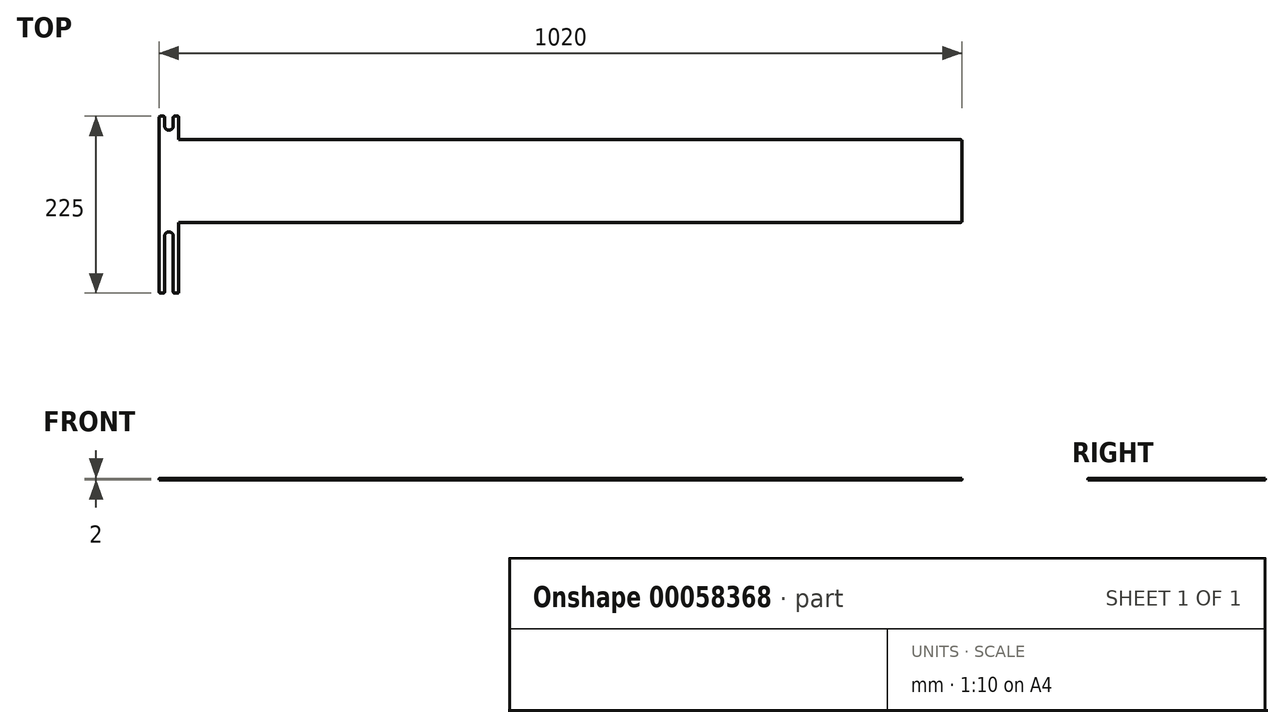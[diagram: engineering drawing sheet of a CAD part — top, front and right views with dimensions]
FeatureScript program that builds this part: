
annotation { "Feature Type Name" : "Feature", "Feature Type Description" : "" }
export const myFeature = defineFeature(function(context is Context, id is Id, definition is map)
    precondition{}
    {
        {
            var Q0;
            Q0=qCreatedBy(makeId("Top.planeOp"),FACE);
            var sketch = newSketch(context, id + "F0", { "sketchPlane" : qUnion([Q0])});
            skLineSegment(sketch, "E0.bottom", {"start": v(-510, 52.5) * mm, "end": v(510, 52.5) * mm});
            skLineSegment(sketch, "E0.top", {"start": v(-510, -52.5) * mm, "end": v(510, -52.5) * mm});
            skLineSegment(sketch, "E0.left", {"start": v(-510, 52.5) * mm, "end": v(-510, -52.5) * mm});
            skLineSegment(sketch, "E0.right", {"start": v(510, 52.5) * mm, "end": v(510, -52.5) * mm});
            skSolve(sketch);
        }
        {
            var Q0;
            Q0=makeQuery(id+"F0.imprint","IMPRINT",FACE,{"disambiguationData":[TD([[makeQuery(id+"F0.imprint","IMPRINT",EDGE,{"derivedFrom":sQuery(id+"F0.wireOp",EDGE,"E0.bottom")}),-1.0]])]});
            extrude(context, id + "F1", {"entities" : qUnion([Q0]), "depth" : 2 * mm});
        }
        {
            var Q0;
            Q0=makeQuery(id+"F1.opExtrude","CAP_FACE",FACE,{"disambiguationData":[OSD([sQuery(id+"F0.wireOp",EDGE,"E0.bottom"),sQuery(id+"F0.wireOp",EDGE,"E0.top"),sQuery(id+"F0.wireOp",EDGE,"E0.left"),sQuery(id+"F0.wireOp",EDGE,"E0.right")])],"isStart":false});
            var sketch = newSketch(context, id + "F2", { "sketchPlane" : qUnion([Q0])});
            skLineSegment(sketch, "E1", {"start": v(-510, -52.5) * mm, "end": v(-510, -142.5) * mm});
            skLineSegment(sketch, "E2", {"start": v(-510, -142.5) * mm, "end": v(-503, -142.5) * mm});
            skLineSegment(sketch, "E3", {"start": v(-503, -142.5) * mm, "end": v(-503, -64.5) * mm});
            skLineSegment(sketch, "E4", {"start": v(-503, -64.5) * mm, "end": v(-492.1, -64.5) * mm});
            skLineSegment(sketch, "E5", {"start": v(-492.1, -64.5) * mm, "end": v(-492.1, -142.5) * mm});
            skLineSegment(sketch, "E6", {"start": v(-492.1, -142.5) * mm, "end": v(-485, -142.5) * mm});
            skLineSegment(sketch, "E7", {"start": v(-485, -142.5) * mm, "end": v(-485, -52.5) * mm});
            skLineSegment(sketch, "E8", {"start": v(-485, -52.5) * mm, "end": v(-510, -52.5) * mm});
            skSolve(sketch);
        }
        {
            var Q0;
            Q0=makeQuery(id+"F2.imprint","IMPRINT",FACE,{"disambiguationData":[TD([[makeQuery(id+"F2.imprint","IMPRINT",EDGE,{"derivedFrom":sQuery(id+"F2.wireOp",EDGE,"E1")}),1.0]])]});
            extrude(context, id + "F3", {"entities" : qUnion([Q0]), "operationType" : NewBodyOperationType.ADD, "oppositeDirection" : true, "depth" : 2 * mm});
        }
        {
            var Q0;
            Q0=makeQuery(id+"F3.boolean.opBoolean","MERGE",FACE,{"derivedFrom":[makeQuery(id+"F1.opExtrude","CAP_FACE",FACE,{"disambiguationData":[OSD([sQuery(id+"F0.wireOp",EDGE,"E0.bottom"),sQuery(id+"F0.wireOp",EDGE,"E0.top"),sQuery(id+"F0.wireOp",EDGE,"E0.left"),sQuery(id+"F0.wireOp",EDGE,"E0.right")])],"isStart":false}),makeQuery(id+"F3.opExtrude","CAP_FACE",FACE,{"disambiguationData":[OSD([sQuery(id+"F2.wireOp",EDGE,"E1"),sQuery(id+"F2.wireOp",EDGE,"E2"),sQuery(id+"F2.wireOp",EDGE,"E3"),sQuery(id+"F2.wireOp",EDGE,"E4"),sQuery(id+"F2.wireOp",EDGE,"E5"),sQuery(id+"F2.wireOp",EDGE,"E6"),sQuery(id+"F2.wireOp",EDGE,"E7"),sQuery(id+"F2.wireOp",EDGE,"E8")])],"isStart":true})]});
            var sketch = newSketch(context, id + "F4", { "sketchPlane" : qUnion([Q0])});
            skLineSegment(sketch, "E9", {"start": v(0, 0) * mm, "end": v(-510, 0) * mm, "construction": true});
            skSolve(sketch);
        }
        {
            var Q0;
            Q0=makeQuery(id+"F1.opExtrude","SWEPT_BODY",BODY,{"disambiguationData":[OSD([sQuery(id+"F0.wireOp",EDGE,"E0.bottom"),sQuery(id+"F0.wireOp",EDGE,"E0.top"),sQuery(id+"F0.wireOp",EDGE,"E0.left"),sQuery(id+"F0.wireOp",EDGE,"E0.right")])]});
            var Q1;
            Q1=qCreatedBy(makeId("Front.planeOp"),FACE);
            mirror(context, id + "F5", {"operationType" : NewBodyOperationType.ADD, "entities" : qUnion([Q0]), "mirrorPlane" : qUnion([Q1])});
        }
        {
            var Q0;
            Q0=makeQuery(id+"F4.imprint","IMPRINT",FACE,{"disambiguationData":[TD([[makeQuery(id+"F4.imprint","IMPRINT",EDGE,{"derivedFrom":makeQuery(id+"F1.opExtrude","CAP_EDGE",EDGE,{"disambiguationData":[OSD([sQuery(id+"F0.wireOp",EDGE,"E0.bottom")])],"isStart":false})}),-1.0]])]});
            var sketch = newSketch(context, id + "F6", { "sketchPlane" : qUnion([Q0])});
            skLineSegment(sketch, "E10.bottom", {"start": v(-535.27, 162.5) * mm, "end": v(-465.98, 162.5) * mm});
            skLineSegment(sketch, "E10.top", {"start": v(-535.27, 82.5) * mm, "end": v(-465.98, 82.5) * mm});
            skLineSegment(sketch, "E10.left", {"start": v(-535.27, 162.5) * mm, "end": v(-535.27, 82.5) * mm});
            skLineSegment(sketch, "E10.right", {"start": v(-465.98, 162.5) * mm, "end": v(-465.98, 82.5) * mm});
            skSolve(sketch);
        }
        {
            var Q0;
            Q0=makeQuery(id+"F6.imprint","IMPRINT",FACE,{"disambiguationData":[TD([[makeQuery(id+"F6.imprint","IMPRINT",EDGE,{"derivedFrom":sQuery(id+"F6.wireOp",EDGE,"E10.bottom")}),-1.0]])]});
            extrude(context, id + "F7", {"entities" : qUnion([Q0]), "operationType" : NewBodyOperationType.REMOVE, "endBound" : BoundingType.THROUGH_ALL, "oppositeDirection" : true, "depth" : 25 * mm});
        }
        {
            var Q0;
            Q0=makeQuery(id+"F3.opExtrude","SWEPT_EDGE",EDGE,{"disambiguationData":[OSD([sQuery(id+"F2.wireOp",EDGE,"E3"),sQuery(id+"F2.wireOp",EDGE,"E4")])]});
            var Q1;
            Q1=makeQuery(id+"F3.opExtrude","SWEPT_EDGE",EDGE,{"disambiguationData":[OSD([sQuery(id+"F2.wireOp",EDGE,"E4"),sQuery(id+"F2.wireOp",EDGE,"E5")])]});
            var Q2;
            Q2=makeQuery(id+"F5.opPattern","COPY",EDGE,{"derivedFrom":makeQuery(id+"F3.opExtrude","SWEPT_EDGE",EDGE,{"disambiguationData":[OSD([sQuery(id+"F2.wireOp",EDGE,"E3"),sQuery(id+"F2.wireOp",EDGE,"E4")])]}),"instanceName":"1"});
            var Q3;
            Q3=makeQuery(id+"F5.opPattern","COPY",EDGE,{"derivedFrom":makeQuery(id+"F3.opExtrude","SWEPT_EDGE",EDGE,{"disambiguationData":[OSD([sQuery(id+"F2.wireOp",EDGE,"E4"),sQuery(id+"F2.wireOp",EDGE,"E5")])]}),"instanceName":"1"});
            fillet(context, id + "F8", {"entities" : qUnion([Q0, Q1, Q2, Q3]), "radius" : 5.45 * mm, "tangentPropagation" : true, "allowEdgeOverflow" : false});
        }
        {
            var Q0;
            Q0=makeQuery(id+"F5.opPattern","COPY",EDGE,{"derivedFrom":makeQuery(id+"F3.opExtrude","SWEPT_EDGE",EDGE,{"disambiguationData":[OSD([sQuery(id+"F0.wireOp",EDGE,"E0.top"),sQuery(id+"F2.wireOp",EDGE,"E7"),sQuery(id+"F2.wireOp",EDGE,"E8")])]}),"instanceName":"1"});
            var Q1;
            Q1=makeQuery(id+"F7.boolean.opBoolean","INTERSECT",EDGE,{"derivedFrom":[makeQuery(id+"F5.opPattern","COPY",FACE,{"derivedFrom":makeQuery(id+"F3.opExtrude","SWEPT_FACE",FACE,{"disambiguationData":[OSD([sQuery(id+"F2.wireOp",EDGE,"E7")])]}),"instanceName":"1"}),makeQuery(id+"F7.opExtrude","SWEPT_FACE",FACE,{"disambiguationData":[OSD([sQuery(id+"F6.wireOp",EDGE,"E10.top")])]})]});
            var Q2;
            Q2=makeQuery(id+"F7.boolean.opBoolean","INTERSECT",EDGE,{"derivedFrom":[makeQuery(id+"F5.opPattern","COPY",FACE,{"derivedFrom":makeQuery(id+"F3.opExtrude","SWEPT_FACE",FACE,{"disambiguationData":[OSD([sQuery(id+"F2.wireOp",EDGE,"E5")])]}),"instanceName":"1"}),makeQuery(id+"F7.opExtrude","SWEPT_FACE",FACE,{"disambiguationData":[OSD([sQuery(id+"F6.wireOp",EDGE,"E10.top")])]})]});
            var Q3;
            Q3=makeQuery(id+"F7.boolean.opBoolean","INTERSECT",EDGE,{"derivedFrom":[makeQuery(id+"F5.opPattern","COPY",FACE,{"derivedFrom":makeQuery(id+"F3.opExtrude","SWEPT_FACE",FACE,{"disambiguationData":[OSD([sQuery(id+"F2.wireOp",EDGE,"E3")])]}),"instanceName":"1"}),makeQuery(id+"F7.opExtrude","SWEPT_FACE",FACE,{"disambiguationData":[OSD([sQuery(id+"F6.wireOp",EDGE,"E10.top")])]})]});
            var Q4;
            {var subQ0=makeQuery(id+"F3.boolean.opBoolean","MERGE",FACE,{"derivedFrom":[makeQuery(id+"F1.opExtrude","SWEPT_FACE",FACE,{"disambiguationData":[OSD([sQuery(id+"F0.wireOp",EDGE,"E0.left")])]}),makeQuery(id+"F3.opExtrude","SWEPT_FACE",FACE,{"disambiguationData":[OSD([sQuery(id+"F2.wireOp",EDGE,"E1")])]})]});Q4=makeQuery(id+"F7.boolean.opBoolean","INTERSECT",EDGE,{"derivedFrom":[makeQuery(id+"F5.boolean.opBoolean","MERGE",FACE,{"derivedFrom":[subQ0,makeQuery(id+"F5.opPattern","COPY",FACE,{"derivedFrom":subQ0,"instanceName":"1"})]}),makeQuery(id+"F7.opExtrude","SWEPT_FACE",FACE,{"disambiguationData":[OSD([sQuery(id+"F6.wireOp",EDGE,"E10.top")])]})]});}
            var Q5;
            Q5=makeQuery(id+"F3.opExtrude","SWEPT_EDGE",EDGE,{"disambiguationData":[OSD([sQuery(id+"F0.wireOp",EDGE,"E0.top"),sQuery(id+"F2.wireOp",EDGE,"E7"),sQuery(id+"F2.wireOp",EDGE,"E8")])]});
            var Q6;
            Q6=makeQuery(id+"F3.opExtrude","SWEPT_EDGE",EDGE,{"disambiguationData":[OSD([sQuery(id+"F2.wireOp",EDGE,"E6"),sQuery(id+"F2.wireOp",EDGE,"E7")])]});
            var Q7;
            Q7=makeQuery(id+"F3.opExtrude","SWEPT_EDGE",EDGE,{"disambiguationData":[OSD([sQuery(id+"F2.wireOp",EDGE,"E5"),sQuery(id+"F2.wireOp",EDGE,"E6")])]});
            var Q8;
            Q8=makeQuery(id+"F3.opExtrude","SWEPT_EDGE",EDGE,{"disambiguationData":[OSD([sQuery(id+"F2.wireOp",EDGE,"E2"),sQuery(id+"F2.wireOp",EDGE,"E3")])]});
            var Q9;
            Q9=makeQuery(id+"F3.opExtrude","SWEPT_EDGE",EDGE,{"disambiguationData":[OSD([sQuery(id+"F2.wireOp",EDGE,"E1"),sQuery(id+"F2.wireOp",EDGE,"E2")])]});
            var Q10;
            Q10=makeQuery(id+"F1.opExtrude","SWEPT_EDGE",EDGE,{"disambiguationData":[OSD([sQuery(id+"F0.wireOp",EDGE,"E0.top"),sQuery(id+"F0.wireOp",EDGE,"E0.right")])]});
            var Q11;
            Q11=makeQuery(id+"F1.opExtrude","SWEPT_EDGE",EDGE,{"disambiguationData":[OSD([sQuery(id+"F0.wireOp",EDGE,"E0.bottom"),sQuery(id+"F0.wireOp",EDGE,"E0.right")])]});
            fillet(context, id + "F9", {"entities" : qUnion([Q0, Q1, Q2, Q3, Q4, Q5, Q6, Q7, Q8, Q9, Q10, Q11]), "radius" : 2 * mm, "tangentPropagation" : true, "allowEdgeOverflow" : false});
        }
    });
